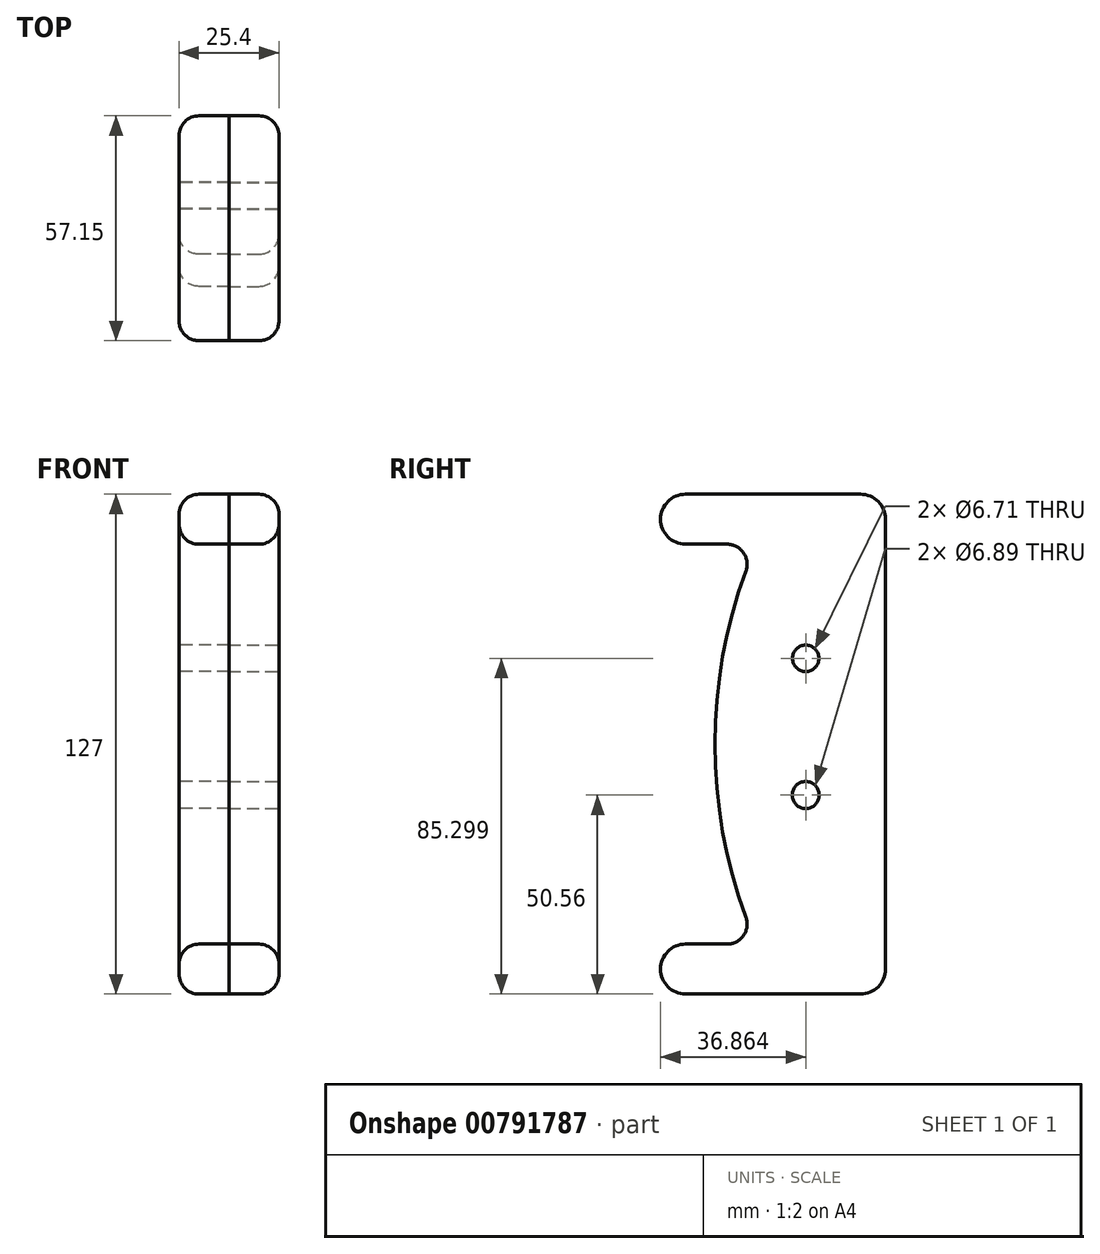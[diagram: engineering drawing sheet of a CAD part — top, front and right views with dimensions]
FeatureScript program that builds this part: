
annotation { "Feature Type Name" : "Feature", "Feature Type Description" : "" }
export const myFeature = defineFeature(function(context is Context, id is Id, definition is map)
    precondition{}
    {
        {
            var Q0;
            Q0=qCreatedBy(makeId("Right.planeOp"),FACE);
            var sketch = newSketch(context, id + "F0", { "sketchPlane" : qUnion([Q0])});
            skLineSegment(sketch, "E0", {"start": v(23.33, 47.25) * mm, "end": v(23.33, -67.05) * mm});
            skLineSegment(sketch, "E1", {"start": v(16.98, -73.4) * mm, "end": v(-27.47, -73.4) * mm});
            skLineSegment(sketch, "E2", {"start": v(-33.82, -67.05) * mm, "end": v(-33.82, -67.05) * mm});
            skLineSegment(sketch, "E3", {"start": v(-27.47, -60.7) * mm, "end": v(-9.42, -60.7) * mm});
            skLineSegment(sketch, "E4", {"start": v(-9.42, -60.7) * mm, "end": v(-9.42, 40.9) * mm});
            skLineSegment(sketch, "E5", {"start": v(-9.42, 40.9) * mm, "end": v(-27.47, 40.9) * mm});
            skLineSegment(sketch, "E6", {"start": v(-33.82, 47.25) * mm, "end": v(-33.82, 47.25) * mm});
            skLineSegment(sketch, "E7", {"start": v(-27.47, 53.6) * mm, "end": v(16.98, 53.6) * mm});
            skCircle(sketch, "E8", {"center": v(3.04, 11.9) * mm, "radius": 3.36 * mm});
            skCircle(sketch, "E9", {"center": v(3.04, -22.84) * mm, "radius": 3.44 * mm});
            skPoint(sketch, "E10.visualSharp", {"position": v(-33.82, 53.6) * mm});
            skArc(sketch, "E10.filletArc", {"start": v(-27.47, 53.6) * mm, "mid": v(-31.96, 51.74) * mm, "end": v(-33.82, 47.25) * mm});
            skPoint(sketch, "E11.visualSharp", {"position": v(-33.82, 40.9) * mm});
            skArc(sketch, "E11.filletArc", {"start": v(-33.82, 47.25) * mm, "mid": v(-31.96, 42.75) * mm, "end": v(-27.47, 40.9) * mm});
            skPoint(sketch, "E12.visualSharp", {"position": v(23.33, 53.6) * mm});
            skArc(sketch, "E12.filletArc", {"start": v(23.33, 47.25) * mm, "mid": v(21.47, 51.74) * mm, "end": v(16.98, 53.6) * mm});
            skPoint(sketch, "E13.visualSharp", {"position": v(23.33, -73.4) * mm});
            skArc(sketch, "E13.filletArc", {"start": v(16.98, -73.4) * mm, "mid": v(21.47, -71.55) * mm, "end": v(23.33, -67.05) * mm});
            skPoint(sketch, "E14.visualSharp", {"position": v(-33.82, -73.4) * mm});
            skArc(sketch, "E14.filletArc", {"start": v(-33.82, -67.05) * mm, "mid": v(-31.96, -71.55) * mm, "end": v(-27.47, -73.4) * mm});
            skPoint(sketch, "E15.visualSharp", {"position": v(-33.82, -60.7) * mm});
            skArc(sketch, "E15.filletArc", {"start": v(-27.47, -60.7) * mm, "mid": v(-31.96, -62.56) * mm, "end": v(-33.82, -67.05) * mm});
            skPoint(sketch, "E16.visualSharp", {"position": v(-9.42, -60.7) * mm});
            skLineSegment(sketch, "E16.filletArc", {"start": v(-9.42, -60.7) * mm, "end": v(-9.42, -60.7) * mm});
            skPoint(sketch, "E17.visualSharp", {"position": v(-9.42, 40.9) * mm});
            skLineSegment(sketch, "E17.filletArc", {"start": v(-9.42, 40.9) * mm, "end": v(-9.42, 40.9) * mm});
            skArc(sketch, "E18", {"start": v(-9.42, 40.9) * mm, "mid": v(-20, -9.9) * mm, "end": v(-9.42, -60.7) * mm});
            skSolve(sketch);
        }
        {
            var Q0;
            Q0=qSketchRegion(id+"F0",true);
            extrude(context, id + "F1", {"entities" : qUnion([Q0]), "depth" : 12.7 * mm});
        }
        {
            var Q0;
            Q0=makeQuery(id+"F1.opExtrude","CAP_EDGE",EDGE,{"disambiguationData":[OSD([sQuery(id+"F0.wireOp",EDGE,"E7")])],"isStart":true});
            var Q1;
            Q1=makeQuery(id+"F1.opExtrude","CAP_EDGE",EDGE,{"disambiguationData":[OSD([sQuery(id+"F0.wireOp",EDGE,"E18")])],"isStart":true});
            var Q2;
            Q2=makeQuery(id+"F1.opExtrude","SWEPT_EDGE",EDGE,{"disambiguationData":[OSD([sQuery(id+"F0.wireOp",EDGE,"E4"),sQuery(id+"F0.wireOp",EDGE,"E5"),sQuery(id+"F0.wireOp",EDGE,"E18")])]});
            var Q3;
            Q3=makeQuery(id+"F1.opExtrude","SWEPT_EDGE",EDGE,{"disambiguationData":[OSD([sQuery(id+"F0.wireOp",EDGE,"E3"),sQuery(id+"F0.wireOp",EDGE,"E4"),sQuery(id+"F0.wireOp",EDGE,"E18")])]});
            fillet(context, id + "F2", {"entities" : qUnion([Q0, Q1, Q2, Q3]), "radius" : 5.08 * mm, "tangentPropagation" : true, "allowEdgeOverflow" : false});
        }
        {
            var Q0;
            Q0=makeQuery(id+"F1.opExtrude","SWEPT_BODY",BODY,{"disambiguationData":[OSD([sQuery(id+"F0.wireOp",EDGE,"E0"),sQuery(id+"F0.wireOp",EDGE,"E1"),sQuery(id+"F0.wireOp",EDGE,"E3"),sQuery(id+"F0.wireOp",EDGE,"E4"),sQuery(id+"F0.wireOp",EDGE,"E5"),sQuery(id+"F0.wireOp",EDGE,"E7"),sQuery(id+"F0.wireOp",EDGE,"E8"),sQuery(id+"F0.wireOp",EDGE,"E9"),sQuery(id+"F0.wireOp",EDGE,"E10.filletArc"),sQuery(id+"F0.wireOp",EDGE,"E11.filletArc"),sQuery(id+"F0.wireOp",EDGE,"E12.filletArc"),sQuery(id+"F0.wireOp",EDGE,"E13.filletArc"),sQuery(id+"F0.wireOp",EDGE,"E14.filletArc"),sQuery(id+"F0.wireOp",EDGE,"E15.filletArc")])]});
            var Q1;
            Q1=makeQuery(id+"F1.opExtrude","CAP_FACE",FACE,{"disambiguationData":[OSD([sQuery(id+"F0.wireOp",EDGE,"E0"),sQuery(id+"F0.wireOp",EDGE,"E1"),sQuery(id+"F0.wireOp",EDGE,"E3"),sQuery(id+"F0.wireOp",EDGE,"E4"),sQuery(id+"F0.wireOp",EDGE,"E5"),sQuery(id+"F0.wireOp",EDGE,"E7"),sQuery(id+"F0.wireOp",EDGE,"E8"),sQuery(id+"F0.wireOp",EDGE,"E9"),sQuery(id+"F0.wireOp",EDGE,"E10.filletArc"),sQuery(id+"F0.wireOp",EDGE,"E11.filletArc"),sQuery(id+"F0.wireOp",EDGE,"E12.filletArc"),sQuery(id+"F0.wireOp",EDGE,"E13.filletArc"),sQuery(id+"F0.wireOp",EDGE,"E14.filletArc"),sQuery(id+"F0.wireOp",EDGE,"E15.filletArc")])],"isStart":false});
            mirror(context, id + "F3", {"entities" : qUnion([Q0]), "mirrorPlane" : qUnion([Q1])});
        }
    });
